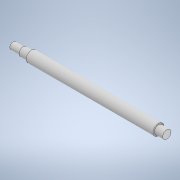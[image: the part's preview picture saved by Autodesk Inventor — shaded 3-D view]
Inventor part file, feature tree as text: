
AUTODESK INVENTOR PART (.ipt)
format: ipt  version: 2020.2 (Build 242310000, 310)  size: 112,640 bytes
history: native  units: mm
features: other x2, sketch x1
ambient origin geometry x8: Origin, YZ Plane, XZ Plane, XY Plane, X Axis, Y Axis, Z Axis, Center Point
bodies: Body1 (feature_tree)
feature tree (3):
  other  "Sólido1"
  other  "Revolução1"
  sketch  "Esboço1"  dims[d0=6.0mm d1=2.0mm d2=5.0mm d3=2.5mm d4=1.0mm d5=3.25mm d6=3.25mm d7=75.0mm d8=5.0mm d9=2.5mm d10=90.0deg]
